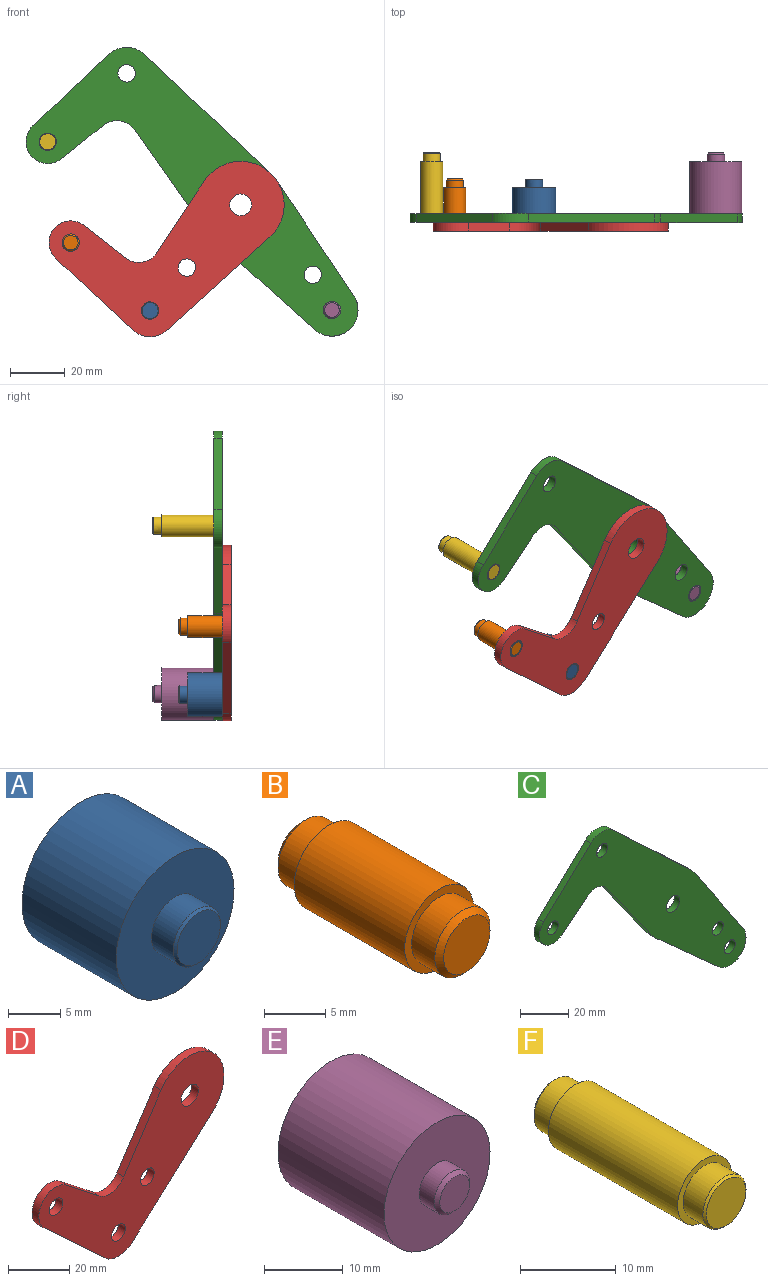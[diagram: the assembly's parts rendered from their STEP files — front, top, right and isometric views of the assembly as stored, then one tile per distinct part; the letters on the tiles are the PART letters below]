
ASSEMBLY  parts=6 mates=5
PART A: 9 faces, bbox 15.9x19.1x15.9 mm
  f0: cylinder r=7.94mm len=15.88mm, axis (0,-1,0), area 633.4mm2, adj f2,f6
  f1: cylinder r=3.17mm len=6.35mm, axis (0,-1,0), area 58.3mm2, adj f2,f4
  f2: plane 15.88x15.88mm, normal (0,-1,0), area 166.3mm2, adj f0,f1
  f3: plane 5.84x5.84mm, normal (0,-1,0), area 26.8mm2, adj f4
  f4: cone r=2.92mm half-angle=45deg, axis (0,1,0), area 6.9mm2, adj f1,f3
  f5: cylinder r=3.17mm len=6.35mm, axis (0,1,0), area 58.3mm2, adj f6,f8
  f6: plane 15.88x15.88mm, normal (0,1,0), area 166.3mm2, adj f0,f5
  f7: plane 5.84x5.84mm, normal (0,1,0), area 26.8mm2, adj f8
  f8: cone r=2.92mm half-angle=45deg, axis (0,-1,0), area 6.9mm2, adj f5,f7
PART B: 9 faces, bbox 8x19.1x8 mm
  f0: cylinder r=3.98mm len=12.7mm, axis (0,-1,0), area 317.2mm2, adj f2,f6
  f1: cylinder r=3.17mm len=6.35mm, axis (0,-1,0), area 53.2mm2, adj f2,f4
  f2: plane 7.95x7.95mm, normal (0,-1,0), area 18mm2, adj f0,f1
  f3: plane 5.33x5.33mm, normal (0,-1,0), area 22.3mm2, adj f4
  f4: cone r=2.67mm half-angle=45deg, axis (0,1,0), area 13.2mm2, adj f1,f3
  f5: cylinder r=3.17mm len=6.35mm, axis (0,1,0), area 53.2mm2, adj f6,f8
  f6: plane 7.95x7.95mm, normal (0,1,0), area 18mm2, adj f0,f5
  f7: plane 5.33x5.33mm, normal (0,1,0), area 22.3mm2, adj f8
  f8: cone r=2.67mm half-angle=45deg, axis (0,-1,0), area 13.2mm2, adj f5,f7
PART C: 19 faces, bbox 121.1x3.2x105.4 mm
  f0: plane 36.5x25.75mm, normal (-0.82,0,-0.58), area 141.8mm2, adj f1,f15,f17,f18
  f1: cylinder r=15.88mm len=3.18mm, axis (0,1,0), area 11.4mm2, adj f0,f2,f17,f18
  f2: plane 37.52x33.65mm, normal (-0.67,0,-0.74), area 160mm2, adj f1,f3,f17,f18
  f3: cylinder r=9.53mm len=15.88mm, axis (0,1,0), area 87.4mm2, adj f2,f4,f17,f18
  f4: plane 41.9x28.01mm, normal (0.83,0,0.56), area 160mm2, adj f3,f5,f17,f18
  f5: cylinder r=15.88mm len=3.18mm, axis (0,1,0), area 11.4mm2, adj f4,f6,f17,f18
  f6: plane 45.96x43.35mm, normal (0.69,0,0.73), area 200.6mm2, adj f5,f7,f17,f18
  f7: cylinder r=9.53mm len=13.07mm, axis (0,1,0), area 45.7mm2, adj f6,f8,f17,f18
  f8: plane 27.69x26.12mm, normal (-0.69,0,0.73), area 120.9mm2, adj f7,f9,f17,f18
  f9: cylinder r=7.94mm len=13.71mm, axis (0,1,0), area 77.1mm2, adj f8,f10,f17,f18
  f10: plane 15.29x12.18mm, normal (0.62,0,-0.78), area 62.1mm2, adj f9,f15,f17,f18
  f11: cylinder r=3.17mm len=6.35mm, axis (0,1,0), area 63.3mm2, adj f17,f18
  f12: cylinder r=3.17mm len=6.35mm, axis (0,1,0), area 63.3mm2, adj f17,f18
  f13: cylinder r=3.97mm len=7.94mm, axis (0,1,0), area 79.2mm2, adj f17,f18
  f14: cylinder r=3.17mm len=6.35mm, axis (0,1,0), area 63.3mm2, adj f17,f18
  f15: cylinder r=7.94mm len=11.43mm, axis (0,1,0), area 41.1mm2, adj f0,f10,f17,f18
  f16: cylinder r=3.17mm len=6.35mm, axis (0,1,0), area 63.3mm2, adj f17,f18
  f17: plane 121.14x105.4mm, normal (0,-1,0), area 3645.8mm2, adj f0,f1,f2,f3,f4,f5,f6,f7
  f18: plane 121.14x105.4mm, normal (0,1,0), area 3645.8mm2, adj f0,f1,f2,f3,f4,f5,f6,f7
PART D: 14 faces, bbox 85.8x3.2x64 mm
  f0: cylinder r=15.88mm len=29.13mm, axis (0,-1,0), area 171mm2, adj f1,f9,f12,f13
  f1: plane 26.22x17.3mm, normal (-0.83,0,0.55), area 99.7mm2, adj f0,f2,f12,f13
  f2: cylinder r=7.94mm len=11.53mm, axis (0,-1,0), area 41.7mm2, adj f1,f3,f12,f13
  f3: plane 14.99x11.8mm, normal (0.62,0,0.79), area 60.6mm2, adj f2,f4,f12,f13
  f4: cylinder r=7.94mm len=13.75mm, axis (0,-1,0), area 77.1mm2, adj f3,f5,f12,f13
  f5: plane 27.85x25.95mm, normal (-0.68,0,-0.73), area 120.9mm2, adj f4,f6,f12,f13
  f6: cylinder r=9.53mm len=12.9mm, axis (0,-1,0), area 45mm2, adj f5,f9,f12,f13
  f7: cylinder r=3.17mm len=6.35mm, axis (0,-1,0), area 63.3mm2, adj f12,f13
  f8: cylinder r=3.17mm len=6.35mm, axis (0,-1,0), area 63.3mm2, adj f12,f13
  f9: plane 37.32x33.88mm, normal (0.67,0,-0.74), area 160mm2, adj f0,f6,f12,f13
  f10: cylinder r=3.97mm len=7.94mm, axis (0,-1,0), area 79.2mm2, adj f12,f13
  f11: cylinder r=3.17mm len=6.35mm, axis (0,-1,0), area 63.3mm2, adj f12,f13
  f12: plane 85.8x63.98mm, normal (0,1,0), area 2309.4mm2, adj f0,f1,f2,f3,f4,f5,f6,f7
  f13: plane 85.8x63.98mm, normal (0,-1,0), area 2309.4mm2, adj f0,f1,f2,f3,f4,f5,f6,f7
PART E: 9 faces, bbox 19.1x25.4x19.1 mm
  f0: cylinder r=9.53mm len=19.05mm, axis (0,-1,0), area 1140.1mm2, adj f2,f6
  f1: cylinder r=3.17mm len=6.35mm, axis (0,1,0), area 53.2mm2, adj f2,f4
  f2: plane 19.05x19.05mm, normal (0,-1,0), area 253.4mm2, adj f0,f1
  f3: plane 5.33x5.33mm, normal (0,-1,0), area 22.3mm2, adj f4
  f4: cone r=2.67mm half-angle=45deg, axis (0,1,0), area 13.2mm2, adj f1,f3
  f5: cylinder r=3.17mm len=6.35mm, axis (0,-1,0), area 53.2mm2, adj f6,f8
  f6: plane 19.05x19.05mm, normal (0,1,0), area 253.4mm2, adj f0,f5
  f7: plane 5.33x5.33mm, normal (0,1,0), area 22.3mm2, adj f8
  f8: cone r=2.67mm half-angle=45deg, axis (0,-1,0), area 13.2mm2, adj f5,f7
PART F: 9 faces, bbox 8x25.4x8 mm
  f0: cylinder r=3.98mm len=19.05mm, axis (0,-1,0), area 475.8mm2, adj f2,f6
  f1: cylinder r=3.17mm len=6.35mm, axis (0,1,0), area 58.3mm2, adj f2,f4
  f2: plane 7.95x7.95mm, normal (0,-1,0), area 18mm2, adj f0,f1
  f3: plane 5.84x5.84mm, normal (0,-1,0), area 26.8mm2, adj f4
  f4: cone r=2.92mm half-angle=45deg, axis (0,1,0), area 6.9mm2, adj f1,f3
  f5: cylinder r=3.17mm len=6.35mm, axis (0,-1,0), area 58.3mm2, adj f6,f8
  f6: plane 7.95x7.95mm, normal (0,1,0), area 18mm2, adj f0,f5
  f7: plane 5.84x5.84mm, normal (0,1,0), area 26.8mm2, adj f8
  f8: cone r=2.92mm half-angle=45deg, axis (0,-1,0), area 6.9mm2, adj f5,f7
PLACE A t=(-11.51,-19.22,-1.14)mm
PLACE B t=(-11.51,-19.22,-1.14)mm
PLACE C t=(-11.51,-12.87,-1.14)mm fixed
PLACE D t=(-11.51,-19.22,-1.14)mm
PLACE E t=(-11.51,-12.87,-1.14)mm
PLACE F t=(-11.51,-12.87,-1.14)mm
MATE fastened C.f3 <-> E.f0  axis (0,1,0) through (21.78,-12.87,-39.52)mm
MATE fastened A.f0 <-> D.f6  axis (0,-1,0) through (-44.56,-16.04,-39.72)mm
MATE fastened D.f4 <-> B.f0  axis (0,1,0) through (-73.49,-16.04,-14.93)mm
MATE revolute D.f0 <-> C.f1  axis (0,1,0) through (-11.51,-16.04,-1.14)mm
MATE fastened C.f9 <-> F.f0  axis (0,1,0) through (-81.9,-12.87,21.86)mm
